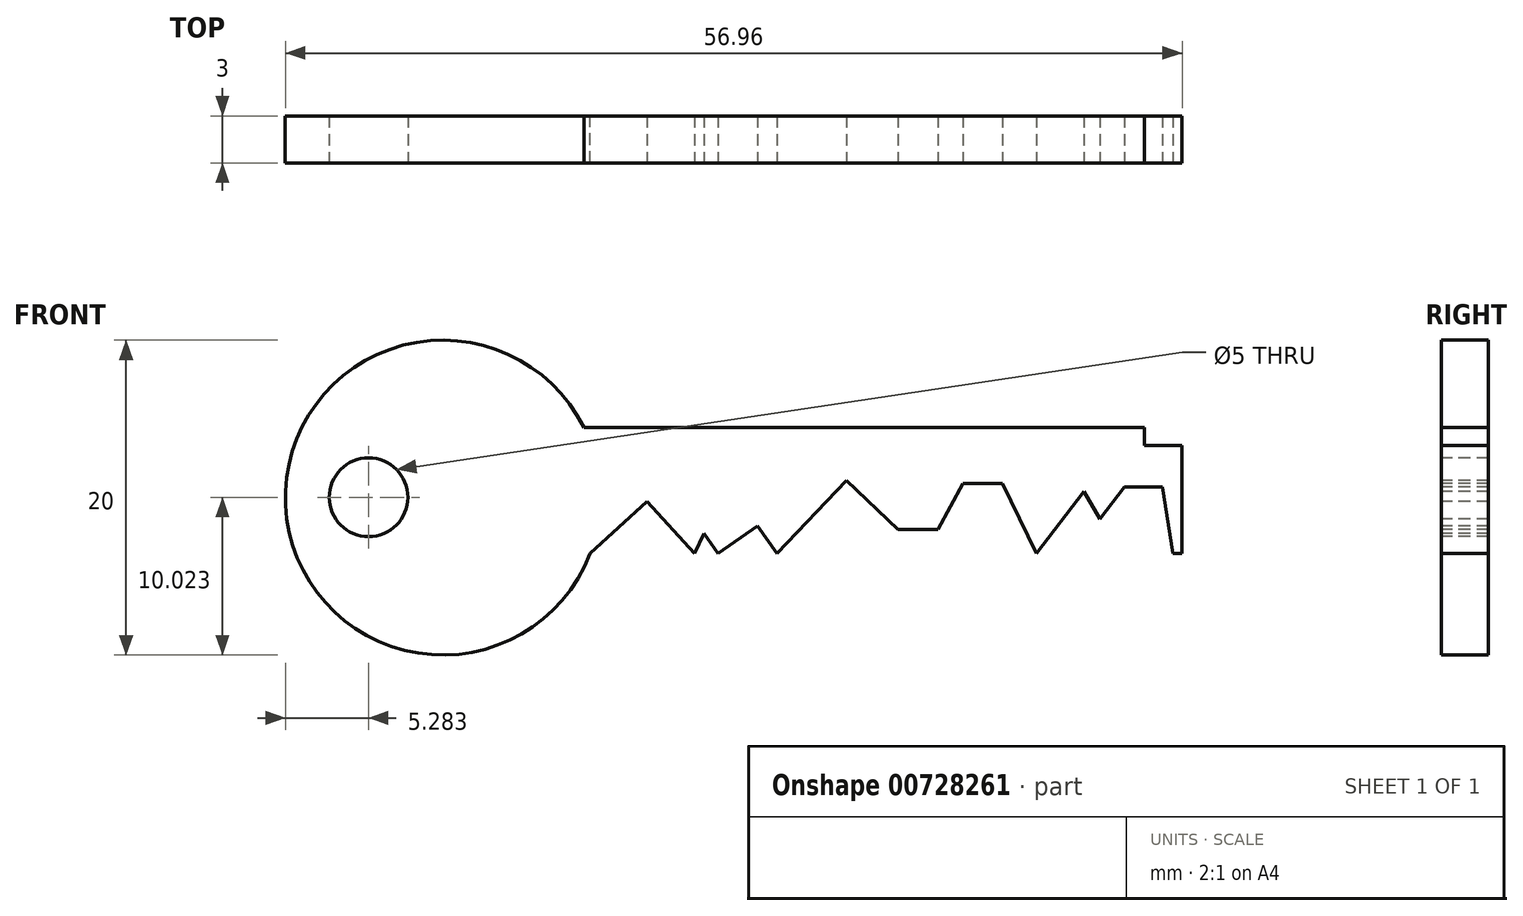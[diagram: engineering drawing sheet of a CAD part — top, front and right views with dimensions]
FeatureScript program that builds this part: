
annotation { "Feature Type Name" : "Feature", "Feature Type Description" : "" }
export const myFeature = defineFeature(function(context is Context, id is Id, definition is map)
    precondition{}
    {
        {
            var Q0;
            Q0=qCreatedBy(makeId("Front.planeOp"),FACE);
            var sketch = newSketch(context, id + "F0", { "sketchPlane" : qUnion([Q0])});
            skCircle(sketch, "E0", {"center": v(-43.94, 16.76) * mm, "radius": 10 * mm});
            skLineSegment(sketch, "E1.bottom", {"start": v(-34.98, 21.2) * mm, "end": v(3.02, 21.2) * mm});
            skLineSegment(sketch, "E1.top", {"start": v(-34.6, 13.2) * mm, "end": v(3.02, 13.2) * mm});
            skLineSegment(sketch, "E1.right", {"start": v(3.02, 21.2) * mm, "end": v(3.02, 13.2) * mm});
            skSolve(sketch);
        }
        {
            var Q0;
            Q0 = qSketchRegion(id + "F0", true);
            extrude(context, id + "F1", {"entities" : qUnion([Q0]), "depth" : 3 * mm, "offsetDistance" : 25 * mm});
        }
        {
            var Q0;
            Q0=makeQuery(id+"F1.opExtrude","CAP_FACE",FACE,{"disambiguationData":[OSD([sQuery(id+"F0.wireOp",EDGE,"E0"),sQuery(id+"F0.wireOp",EDGE,"E1.bottom"),sQuery(id+"F0.wireOp",EDGE,"E1.top"),sQuery(id+"F0.wireOp",EDGE,"E1.right")])],"isStart":false});
            var sketch = newSketch(context, id + "F2", { "sketchPlane" : qUnion([Q0])});
            skLineSegment(sketch, "E2", {"start": v(-34.6, 13.2) * mm, "end": v(-30.97, 16.5) * mm});
            skLineSegment(sketch, "E3", {"start": v(-30.97, 16.5) * mm, "end": v(-27.95, 13.2) * mm});
            skLineSegment(sketch, "E4", {"start": v(-27.95, 13.2) * mm, "end": v(-27.35, 14.48) * mm});
            skLineSegment(sketch, "E5", {"start": v(-27.35, 14.48) * mm, "end": v(-26.46, 13.2) * mm});
            skLineSegment(sketch, "E6", {"start": v(-26.46, 13.2) * mm, "end": v(-23.94, 14.96) * mm});
            skLineSegment(sketch, "E7", {"start": v(-23.94, 14.96) * mm, "end": v(-22.72, 13.2) * mm});
            skLineSegment(sketch, "E8", {"start": v(-22.72, 13.2) * mm, "end": v(-18.29, 17.85) * mm});
            skLineSegment(sketch, "E9", {"start": v(-18.29, 17.85) * mm, "end": v(-15.02, 14.73) * mm});
            skLineSegment(sketch, "E10", {"start": v(-15.02, 14.73) * mm, "end": v(-12.5, 14.73) * mm});
            skLineSegment(sketch, "E11", {"start": v(-12.5, 14.73) * mm, "end": v(-10.9, 17.65) * mm});
            skLineSegment(sketch, "E12", {"start": v(-10.9, 17.65) * mm, "end": v(-8.38, 17.65) * mm});
            skLineSegment(sketch, "E13", {"start": v(-8.38, 17.65) * mm, "end": v(-6.25, 13.2) * mm});
            skLineSegment(sketch, "E14", {"start": v(-6.25, 13.2) * mm, "end": v(-3.23, 17.15) * mm});
            skLineSegment(sketch, "E15", {"start": v(-3.23, 17.15) * mm, "end": v(-2.2, 15.42) * mm});
            skLineSegment(sketch, "E16", {"start": v(-2.2, 15.42) * mm, "end": v(-0.65, 17.43) * mm});
            skLineSegment(sketch, "E17", {"start": v(-0.65, 17.43) * mm, "end": v(1.77, 17.43) * mm});
            skLineSegment(sketch, "E18", {"start": v(1.77, 17.43) * mm, "end": v(2.42, 13.2) * mm});
            skSolve(sketch);
        }
        {
            var Q0;
            Q0 = qSketchRegion(id + "F2", true);
            var Q1;
            {var subQ0=sQuery(id+"F2.wireOp",EDGE,"E2");Q1=makeQuery(id+"F2.imprint","IMPRINT",FACE,{"disambiguationData":[TD([[makeQuery(id+"F2.imprint","IMPRINT",EDGE,{"derivedFrom":subQ0}),-1.0]])]});}
            var Q2;
            {var subQ0=sQuery(id+"F2.wireOp",EDGE,"E4");Q2=makeQuery(id+"F2.imprint","IMPRINT",FACE,{"disambiguationData":[TD([[makeQuery(id+"F2.imprint","IMPRINT",EDGE,{"derivedFrom":subQ0}),-1.0]])]});}
            var Q3;
            {var subQ0=sQuery(id+"F2.wireOp",EDGE,"E6");Q3=makeQuery(id+"F2.imprint","IMPRINT",FACE,{"disambiguationData":[TD([[makeQuery(id+"F2.imprint","IMPRINT",EDGE,{"derivedFrom":subQ0}),-1.0]])]});}
            var Q4;
            {var subQ0=sQuery(id+"F2.wireOp",EDGE,"E8");Q4=makeQuery(id+"F2.imprint","IMPRINT",FACE,{"disambiguationData":[TD([[makeQuery(id+"F2.imprint","IMPRINT",EDGE,{"derivedFrom":subQ0}),-1.0]])]});}
            var Q5;
            {var subQ0=sQuery(id+"F2.wireOp",EDGE,"E14");Q5=makeQuery(id+"F2.imprint","IMPRINT",FACE,{"disambiguationData":[TD([[makeQuery(id+"F2.imprint","IMPRINT",EDGE,{"derivedFrom":subQ0}),-1.0]])]});}
            extrude(context, id + "F3", {"entities" : qUnion([Q0, Q1, Q2, Q3, Q4, Q5]), "operationType" : NewBodyOperationType.REMOVE, "oppositeDirection" : true, "depth" : 25 * mm, "offsetDistance" : 25 * mm});
        }
        {
            var Q0;
            Q0=makeQuery(id+"F1.opExtrude","CAP_FACE",FACE,{"disambiguationData":[OSD([sQuery(id+"F0.wireOp",EDGE,"E0"),sQuery(id+"F0.wireOp",EDGE,"E1.bottom"),sQuery(id+"F0.wireOp",EDGE,"E1.top"),sQuery(id+"F0.wireOp",EDGE,"E1.right")])],"isStart":false});
            var sketch = newSketch(context, id + "F4", { "sketchPlane" : qUnion([Q0])});
            skLineSegment(sketch, "E19.bottom", {"start": v(0.6, 21.2) * mm, "end": v(4.1, 21.2) * mm});
            skLineSegment(sketch, "E19.top", {"start": v(0.6, 20.09) * mm, "end": v(4.1, 20.09) * mm});
            skLineSegment(sketch, "E19.left", {"start": v(0.6, 21.2) * mm, "end": v(0.6, 20.09) * mm});
            skLineSegment(sketch, "E19.right", {"start": v(4.1, 21.2) * mm, "end": v(4.1, 20.09) * mm});
            skSolve(sketch);
        }
        {
            var Q0;
            Q0 = qSketchRegion(id + "F4", true);
            extrude(context, id + "F5", {"entities" : qUnion([Q0]), "operationType" : NewBodyOperationType.REMOVE, "oppositeDirection" : true, "depth" : 25 * mm, "offsetDistance" : 25 * mm});
        }
        {
            var Q0;
            Q0=makeQuery(id+"F1.opExtrude","CAP_FACE",FACE,{"disambiguationData":[OSD([sQuery(id+"F0.wireOp",EDGE,"E0"),sQuery(id+"F0.wireOp",EDGE,"E1.bottom"),sQuery(id+"F0.wireOp",EDGE,"E1.top"),sQuery(id+"F0.wireOp",EDGE,"E1.right")])],"isStart":false});
            var sketch = newSketch(context, id + "F6", { "sketchPlane" : qUnion([Q0])});
            skCircle(sketch, "E20", {"center": v(-48.66, 16.78) * mm, "radius": 2.5 * mm});
            skSolve(sketch);
        }
        {
            var Q0;
            Q0 = qSketchRegion(id + "F6", true);
            extrude(context, id + "F7", {"entities" : qUnion([Q0]), "operationType" : NewBodyOperationType.REMOVE, "oppositeDirection" : true, "depth" : 25 * mm, "offsetDistance" : 25 * mm});
        }
    });
